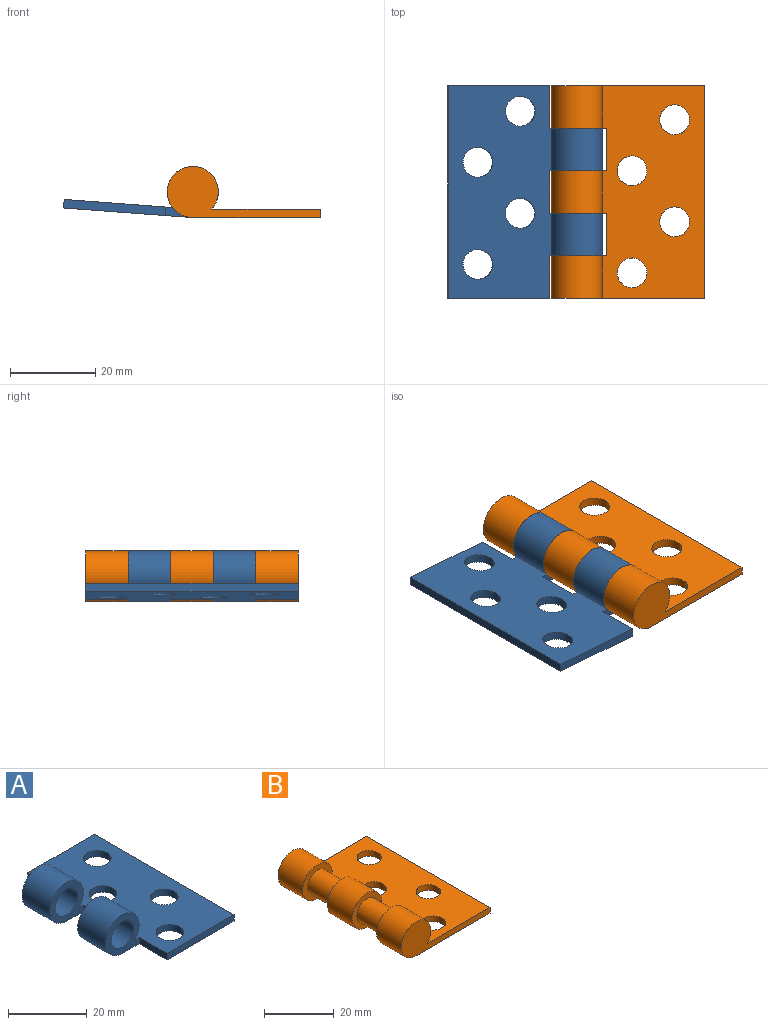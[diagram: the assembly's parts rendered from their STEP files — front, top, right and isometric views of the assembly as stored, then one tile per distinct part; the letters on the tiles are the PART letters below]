
ASSEMBLY  parts=2 mates=1
PART A: 20 faces, bbox 36x50x12 mm
  f0: plane 50x25.53mm, normal (0,0,1), area 1076.1mm2, adj f1,f2,f4,f5,f6,f7,f8,f9
  f1: cylinder r=6mm len=12mm, axis (0,1,0), area 326.5mm2, adj f0,f3,f15,f17
  f2: cylinder r=6mm len=12mm, axis (0,1,0), area 326.5mm2, adj f0,f3,f12,f13
  f3: plane 50x30mm, normal (0,0,-1), area 1165.5mm2, adj f1,f2,f4,f5,f6,f7,f8,f9
  f4: plane 23.98x2mm, normal (0,-1,0), area 48mm2, adj f0,f3,f6,f16
  f5: plane 23.98x2mm, normal (0,1,0), area 48mm2, adj f0,f3,f6,f11
  f6: plane 50x2mm, normal (1,0,0), area 100mm2, adj f0,f3,f4,f5
  f7: cylinder r=3.5mm len=7mm, axis (0,0,1), area 44mm2, adj f0,f3
  f8: cylinder r=3.5mm len=7mm, axis (0,0,1), area 44mm2, adj f0,f3
  f9: cylinder r=3.5mm len=7mm, axis (0,0,1), area 44mm2, adj f0,f3
  f10: cylinder r=3.5mm len=7mm, axis (0,0,1), area 44mm2, adj f0,f3
  f11: plane 10x2mm, normal (-1,0,0), area 20mm2, adj f0,f3,f5,f12
  f12: plane 12.02x12mm, normal (0,1,0), area 68.7mm2, adj f0,f2,f3,f11,f18
  f13: plane 12.02x12mm, normal (0,-1,0), area 68.7mm2, adj f0,f2,f3,f14,f18
  f14: plane 10x2mm, normal (-1,0,0), area 20mm2, adj f0,f3,f13,f15
  f15: plane 12.02x12mm, normal (0,1,0), area 68.7mm2, adj f0,f1,f3,f14,f19
  f16: plane 10x2mm, normal (-1,0,0), area 20mm2, adj f0,f3,f4,f17
  f17: plane 12.02x12mm, normal (0,-1,0), area 68.7mm2, adj f0,f1,f3,f16,f19
  f18: cylinder r=4mm len=10mm, axis (0,1,0), area 251.3mm2, adj f12,f13
  f19: cylinder r=4mm len=10mm, axis (0,1,0), area 251.3mm2, adj f15,f17
PART B: 20 faces, bbox 36x50x12 mm
  f0: plane 50x25.53mm, normal (0,0,1), area 1071.9mm2, adj f1,f2,f4,f5,f6,f7,f8,f9
  f1: cylinder r=6mm len=12mm, axis (0,1,0), area 326.5mm2, adj f0,f3,f14,f15
  f2: cylinder r=6mm len=12mm, axis (0,1,0), area 326.5mm2, adj f0,f3,f7,f12
  f3: plane 50x30mm, normal (0,0,-1), area 1206.1mm2, adj f1,f2,f4,f5,f6,f7,f8,f9
  f4: cylinder r=6mm len=12mm, axis (0,1,0), area 326.5mm2, adj f0,f3,f6,f17
  f5: plane 50x2mm, normal (1,0,0), area 100mm2, adj f0,f3,f6,f7
  f6: plane 36x12mm, normal (0,-1,0), area 166.9mm2, adj f0,f3,f4,f5
  f7: plane 36x12mm, normal (0,1,0), area 166.9mm2, adj f0,f2,f3,f5
  f8: cylinder r=3.5mm len=7mm, axis (0,0,1), area 44mm2, adj f0,f3
  f9: cylinder r=3.5mm len=7mm, axis (0,0,1), area 44mm2, adj f0,f3
  f10: cylinder r=3.5mm len=7mm, axis (0,0,1), area 44mm2, adj f0,f3
  f11: cylinder r=3.5mm len=7mm, axis (0,0,1), area 44mm2, adj f0,f3
  f12: plane 13x12mm, normal (0,-1,0), area 70.6mm2, adj f0,f2,f3,f13,f19
  f13: plane 10x2mm, normal (-1,0,0), area 20mm2, adj f0,f3,f12,f14
  f14: plane 13x12mm, normal (0,1,0), area 70.6mm2, adj f0,f1,f3,f13,f19
  f15: plane 13x12mm, normal (0,-1,0), area 70.6mm2, adj f0,f1,f3,f16,f18
  f16: plane 10x2mm, normal (-1,0,0), area 20mm2, adj f0,f3,f15,f17
  f17: plane 13x12mm, normal (0,1,0), area 70.6mm2, adj f0,f3,f4,f16,f18
  f18: cylinder r=4mm len=10mm, axis (0,1,0), area 251.3mm2, adj f15,f17
  f19: cylinder r=4mm len=10mm, axis (0,1,0), area 251.3mm2, adj f12,f14
PLACE A rot(axis=(-0.04,0,-1),180deg) t=(-30.27,-67.98,8.58)mm
PLACE B t=(-20.08,-17.98,8.2)mm fixed
MATE revolute A.f1 <-> B.f1  axis (0,-1,0) through (-23.89,-27.98,42.7)mm
